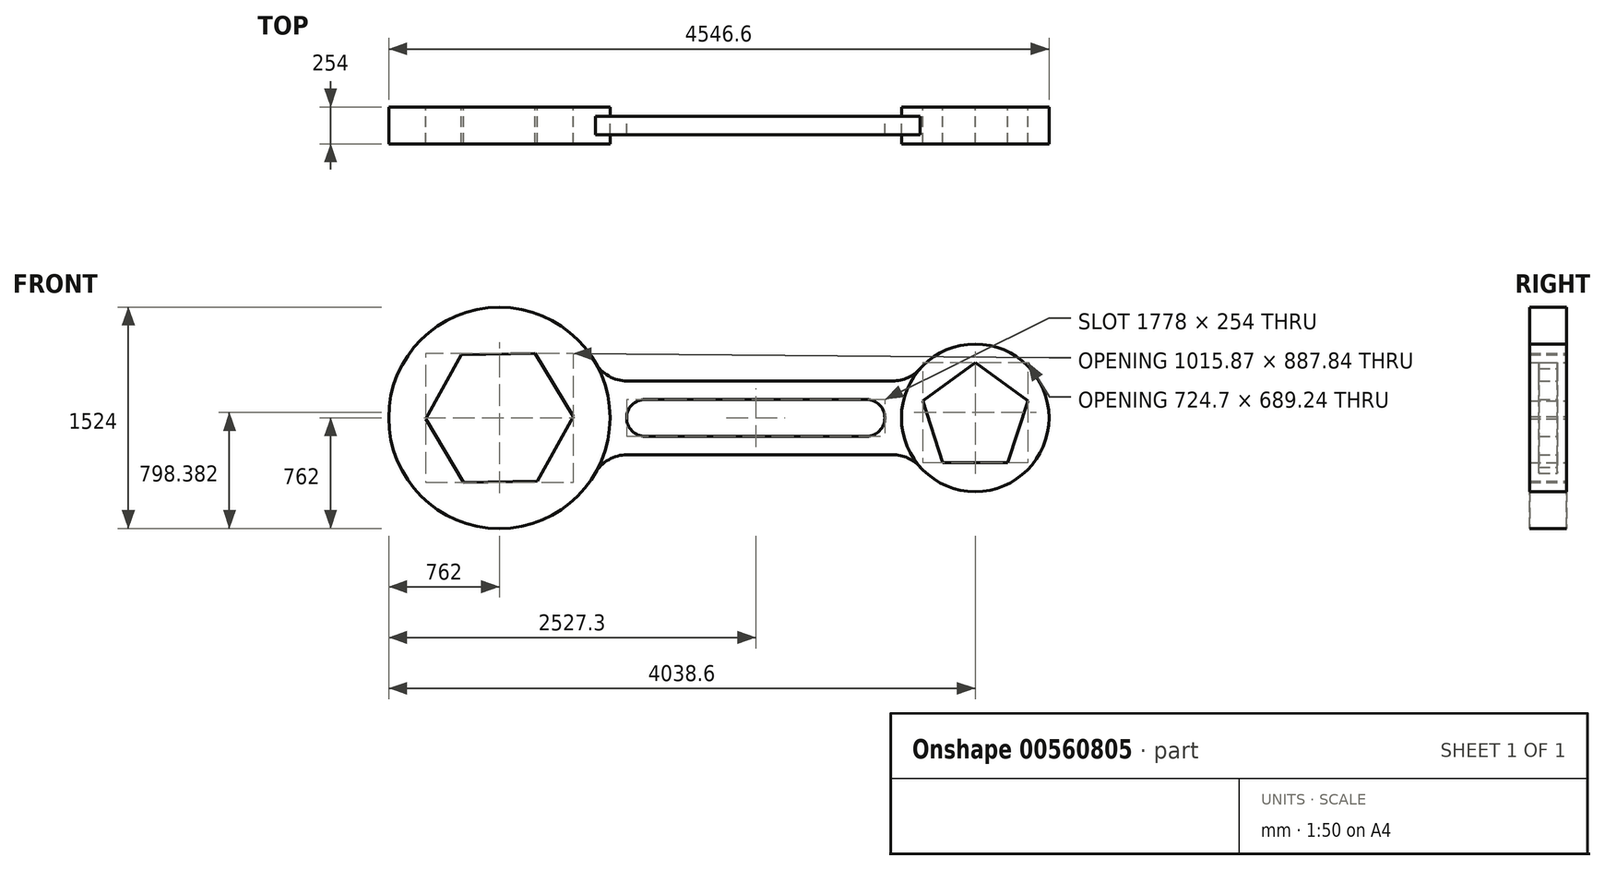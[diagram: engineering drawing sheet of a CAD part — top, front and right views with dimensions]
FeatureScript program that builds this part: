
annotation { "Feature Type Name" : "Feature", "Feature Type Description" : "" }
export const myFeature = defineFeature(function(context is Context, id is Id, definition is map)
    precondition{}
    {
        {
            var Q0;
            Q0=qCreatedBy(makeId("Front.planeOp"),FACE);
            var sketch = newSketch(context, id + "F0", { "sketchPlane" : qUnion([Q0])});
            skCircle(sketch, "E0", {"center": v(0, 0) * mm, "radius": 762 * mm});
            skCircle(sketch, "E1", {"center": v(3276.6, 0) * mm, "radius": 508 * mm});
            skLineSegment(sketch, "E2", {"start": v(1765.3, 127) * mm, "end": v(1003.3, 127) * mm});
            skLineSegment(sketch, "E3", {"start": v(1003.3, -127) * mm, "end": v(2527.3, -127) * mm});
            skLineSegment(sketch, "E4", {"start": v(2527.3, 127) * mm, "end": v(1765.3, 127) * mm});
            skArc(sketch, "E5", {"start": v(1003.3, 127) * mm, "mid": v(876.3, 0) * mm, "end": v(1003.3, -127) * mm});
            skPoint(sketch, "E6.orphan", {"position": v(762, 0) * mm});
            skPoint(sketch, "E7.orphan", {"position": v(2768.6, 0) * mm});
            skArc(sketch, "E8", {"start": v(2527.3, -127) * mm, "mid": v(2654.3, 0) * mm, "end": v(2527.3, 127) * mm});
            skLineSegment(sketch, "E9", {"start": v(1765.3, -254) * mm, "end": v(2708.64, -254) * mm});
            skLineSegment(sketch, "E10", {"start": v(1765.3, -254) * mm, "end": v(879.88, -254) * mm});
            skLineSegment(sketch, "E11", {"start": v(1765.3, 254) * mm, "end": v(2708.64, 254) * mm});
            skLineSegment(sketch, "E12", {"start": v(1765.3, 254) * mm, "end": v(879.88, 254) * mm});
            skArc(sketch, "E13", {"start": v(659.91, 381) * mm, "mid": v(752.88, 288.03) * mm, "end": v(879.88, 254) * mm});
            skArc(sketch, "E14", {"start": v(879.88, -254) * mm, "mid": v(752.88, -288.03) * mm, "end": v(659.91, -381) * mm});
            skArc(sketch, "E15", {"start": v(2708.64, 254) * mm, "mid": v(2812.33, 276.13) * mm, "end": v(2897.96, 338.67) * mm});
            skArc(sketch, "E16", {"start": v(2897.96, -338.67) * mm, "mid": v(2812.33, -276.13) * mm, "end": v(2708.64, -254) * mm});
            skPoint(sketch, "E17.orphan", {"position": v(2654.3, 127) * mm});
            skPoint(sketch, "E18.start.orphan", {"position": v(1765.3, 0) * mm});
            skPoint(sketch, "E19.end.orphan", {"position": v(876.3, 0) * mm});
            skLineSegment(sketch, "E20.0", {"start": v(3276.6, 381) * mm, "end": v(3638.95, 117.74) * mm});
            skLineSegment(sketch, "E20.1", {"start": v(3638.95, 117.74) * mm, "end": v(3500.55, -308.24) * mm});
            skLineSegment(sketch, "E20.2", {"start": v(3500.55, -308.24) * mm, "end": v(3052.65, -308.24) * mm});
            skLineSegment(sketch, "E20.3", {"start": v(3052.65, -308.24) * mm, "end": v(2914.25, 117.74) * mm});
            skLineSegment(sketch, "E20.4", {"start": v(2914.25, 117.74) * mm, "end": v(3276.6, 381) * mm});
            skLineSegment(sketch, "E21.0", {"start": v(-260.96, 435.85) * mm, "end": v(246.98, 443.92) * mm});
            skLineSegment(sketch, "E21.1", {"start": v(246.98, 443.92) * mm, "end": v(507.94, 8.07) * mm});
            skLineSegment(sketch, "E21.2", {"start": v(507.94, 8.07) * mm, "end": v(260.96, -435.85) * mm});
            skLineSegment(sketch, "E21.3", {"start": v(260.96, -435.85) * mm, "end": v(-246.98, -443.92) * mm});
            skLineSegment(sketch, "E21.4", {"start": v(-246.98, -443.92) * mm, "end": v(-507.94, -8.07) * mm});
            skLineSegment(sketch, "E21.5", {"start": v(-507.94, -8.07) * mm, "end": v(-260.96, 435.85) * mm});
            skSolve(sketch);
        }
        {
            var Q0;
            Q0=makeQuery(id+"F0.imprint","IMPRINT",FACE,{"disambiguationData":[TD([[makeQuery(id+"F0.imprint","IMPRINT",EDGE,{"derivedFrom":sQuery(id+"F0.wireOp",EDGE,"E21.0")}),1.0]])]});
            var Q1;
            Q1=makeQuery(id+"F0.imprint","IMPRINT",FACE,{"disambiguationData":[TD([[makeQuery(id+"F0.imprint","IMPRINT",EDGE,{"derivedFrom":sQuery(id+"F0.wireOp",EDGE,"E20.0")}),1.0]])]});
            extrude(context, id + "F1", {"entities" : qUnion([Q0, Q1]), "depth" : 254 * mm, "offsetDistance" : 25.4 * mm, "symmetric" : true});
        }
        {
            var Q0;
            Q0=makeQuery(id+"F0.imprint","IMPRINT",FACE,{"disambiguationData":[TD([[makeQuery(id+"F0.imprint","IMPRINT",EDGE,{"derivedFrom":sQuery(id+"F0.wireOp",EDGE,"E2")}),-1.0]])]});
            extrude(context, id + "F2", {"entities" : qUnion([Q0]), "depth" : 127 * mm, "offsetDistance" : 25.4 * mm, "symmetric" : true});
        }
    });
